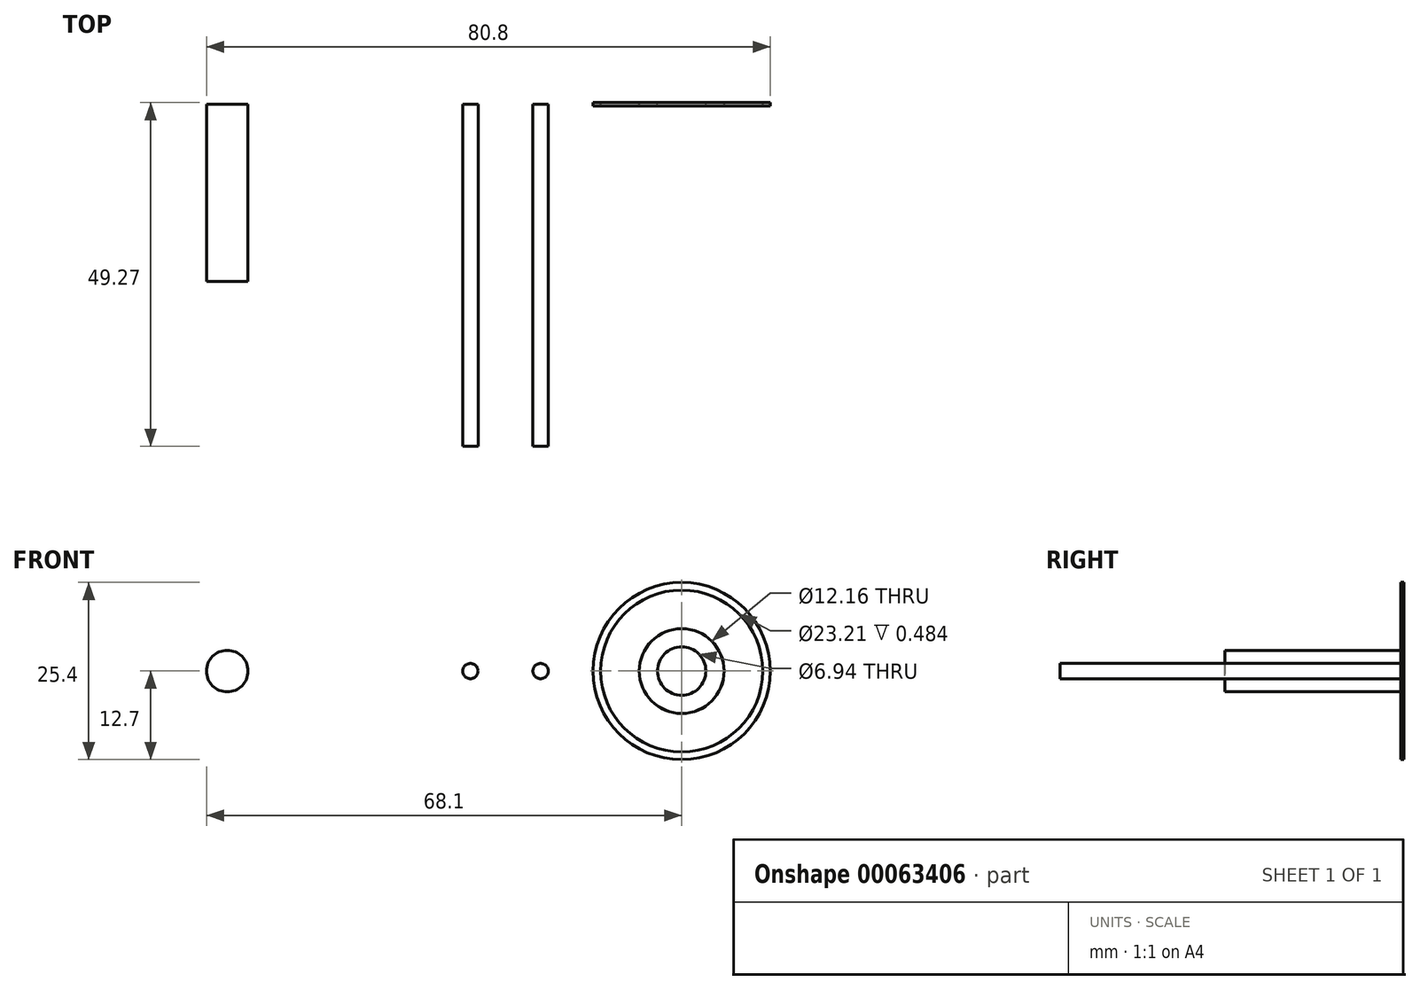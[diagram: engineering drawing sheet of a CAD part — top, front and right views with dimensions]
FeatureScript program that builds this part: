
annotation { "Feature Type Name" : "Feature", "Feature Type Description" : "" }
export const myFeature = defineFeature(function(context is Context, id is Id, definition is map)
    precondition{}
    {
        {
            var Q0;
            Q0=qCreatedBy(makeId("Front.planeOp"),FACE);
            var sketch = newSketch(context, id + "F0", { "sketchPlane" : qUnion([Q0])});
            skCircle(sketch, "E0", {"center": v(0, 0) * mm, "radius": 3.47 * mm});
            skCircle(sketch, "E1", {"center": v(0, 0) * mm, "radius": 6.07 * mm});
            skCircle(sketch, "E2", {"center": v(0, 0) * mm, "radius": 6.08 * mm});
            skCircle(sketch, "E3", {"center": v(0, 0) * mm, "radius": 12.7 * mm});
            skCircle(sketch, "E4", {"center": v(0, 0) * mm, "radius": 11.6 * mm});
            skSolve(sketch);
        }
        {
            var Q0;
            Q0=makeQuery(id+"F0.imprint","IMPRINT",FACE,{"disambiguationData":[TD([[makeQuery(id+"F0.imprint","IMPRINT",EDGE,{"derivedFrom":sQuery(id+"F0.wireOp",EDGE,"E0")}),-1.0]])]});
            extrude(context, id + "F1", {"entities" : qUnion([Q0]), "endBound" : BoundingType.SYMMETRIC, "depth" : 0.48 * mm});
        }
        {
            var Q0;
            Q0=makeQuery(id+"F0.imprint","IMPRINT",FACE,{"disambiguationData":[TD([[makeQuery(id+"F0.imprint","IMPRINT",EDGE,{"derivedFrom":sQuery(id+"F0.wireOp",EDGE,"E2")}),-1.0]])]});
            extrude(context, id + "F2", {"entities" : qUnion([Q0]), "endBound" : BoundingType.SYMMETRIC, "oppositeDirection" : true, "depth" : 0.36 * mm});
        }
        {
            var Q0;
            Q0=makeQuery(id+"F0.imprint","IMPRINT",FACE,{"disambiguationData":[TD([[makeQuery(id+"F0.imprint","IMPRINT",EDGE,{"derivedFrom":sQuery(id+"F0.wireOp",EDGE,"E3")}),1.0]])]});
            extrude(context, id + "F3", {"entities" : qUnion([Q0]), "endBound" : BoundingType.SYMMETRIC, "depth" : 0.48 * mm});
        }
        {
            var Q0;
            Q0=qCreatedBy(makeId("Top.planeOp"),FACE);
            var sketch = newSketch(context, id + "F4", { "sketchPlane" : qUnion([Q0])});
            skLineSegment(sketch, "E5", {"start": v(-68.1, 0) * mm, "end": v(-65.13, 0) * mm});
            skLineSegment(sketch, "E6", {"start": v(-65.13, 0) * mm, "end": v(-65.13, -25.4) * mm});
            skLineSegment(sketch, "E7", {"start": v(-65.13, -25.4) * mm, "end": v(-68.1, -25.4) * mm});
            skLineSegment(sketch, "E8", {"start": v(-68.1, -25.4) * mm, "end": v(-68.1, 0) * mm});
            skSolve(sketch);
        }
        {
            var Q0;
            Q0=makeQuery(id+"F4.imprint","IMPRINT",FACE,{"disambiguationData":[TD([[makeQuery(id+"F4.imprint","IMPRINT",EDGE,{"derivedFrom":sQuery(id+"F4.wireOp",EDGE,"E5")}),-1.0]])]});
            var Q1;
            Q1=sQuery(id+"F4.wireOp",EDGE,"E6");
            revolve(context, id + "F5", {"entities" : qUnion([Q0]), "axis" : qUnion([Q1]), "revolveType" : RevolveType.FULL});
        }
        {
            var Q0;
            Q0=qCreatedBy(makeId("Top.planeOp"),FACE);
            var sketch = newSketch(context, id + "F6", { "sketchPlane" : qUnion([Q0])});
            skLineSegment(sketch, "E9", {"start": v(-30.28, 0) * mm, "end": v(-29.19, 0) * mm});
            skLineSegment(sketch, "E10", {"start": v(-29.19, 0) * mm, "end": v(-29.19, -49.03) * mm});
            skLineSegment(sketch, "E11", {"start": v(-29.19, -49.03) * mm, "end": v(-30.28, -49.03) * mm});
            skLineSegment(sketch, "E12", {"start": v(-30.28, -49.03) * mm, "end": v(-30.28, 0) * mm});
            skSolve(sketch);
        }
        {
            var Q0;
            Q0=makeQuery(id+"F6.imprint","IMPRINT",FACE,{"disambiguationData":[TD([[makeQuery(id+"F6.imprint","IMPRINT",EDGE,{"derivedFrom":sQuery(id+"F6.wireOp",EDGE,"E9")}),-1.0]])]});
            var Q1;
            Q1=sQuery(id+"F6.wireOp",EDGE,"E12");
            revolve(context, id + "F7", {"entities" : qUnion([Q0]), "axis" : qUnion([Q1]), "revolveType" : RevolveType.FULL});
        }
        {
            var Q0;
            Q0=qCreatedBy(makeId("Top.planeOp"),FACE);
            var sketch = newSketch(context, id + "F8", { "sketchPlane" : qUnion([Q0])});
            skLineSegment(sketch, "E13", {"start": v(-20.22, 0) * mm, "end": v(-19.13, 0) * mm});
            skLineSegment(sketch, "E14", {"start": v(-19.13, 0) * mm, "end": v(-19.13, -49.02) * mm});
            skLineSegment(sketch, "E15", {"start": v(-19.13, -49.02) * mm, "end": v(-20.22, -49.02) * mm});
            skLineSegment(sketch, "E16", {"start": v(-20.22, -49.02) * mm, "end": v(-20.22, 0) * mm});
            skSolve(sketch);
        }
        {
            var Q0;
            Q0=makeQuery(id+"F8.imprint","IMPRINT",FACE,{"disambiguationData":[TD([[makeQuery(id+"F8.imprint","IMPRINT",EDGE,{"derivedFrom":sQuery(id+"F8.wireOp",EDGE,"E13")}),-1.0]])]});
            var Q1;
            Q1=sQuery(id+"F8.wireOp",EDGE,"E16");
            revolve(context, id + "F9", {"entities" : qUnion([Q0]), "axis" : qUnion([Q1]), "revolveType" : RevolveType.FULL});
        }
    });
